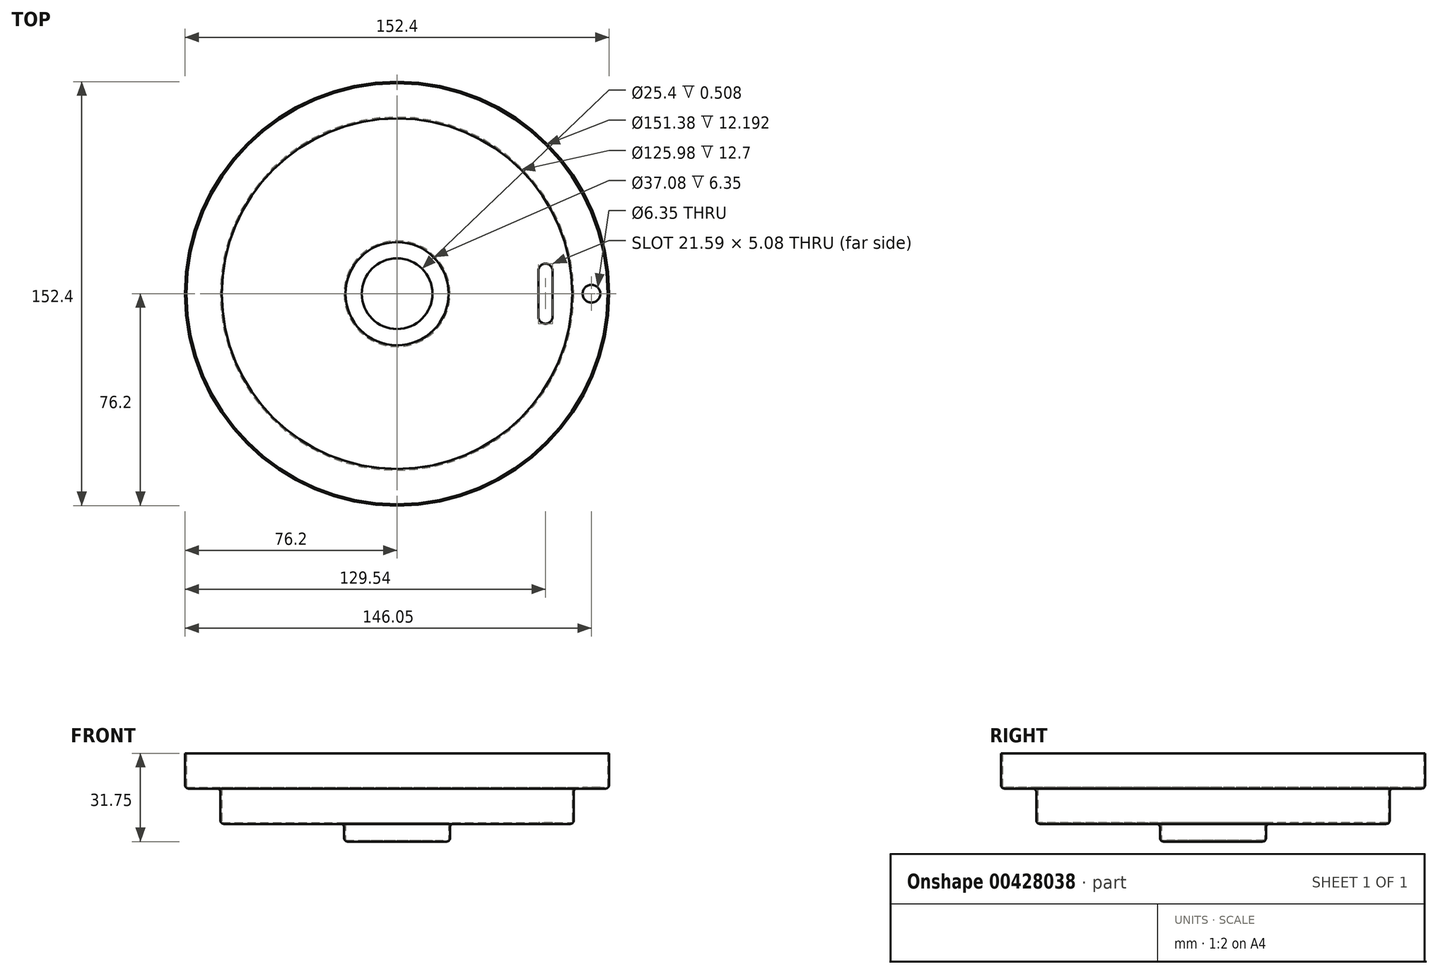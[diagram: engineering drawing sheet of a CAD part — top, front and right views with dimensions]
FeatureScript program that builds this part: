
annotation { "Feature Type Name" : "Feature", "Feature Type Description" : "" }
export const myFeature = defineFeature(function(context is Context, id is Id, definition is map)
    precondition{}
    {
        {
            var Q0;
            Q0=qCreatedBy(makeId("Front.planeOp"),FACE);
            var sketch = newSketch(context, id + "F0", { "sketchPlane" : qUnion([Q0])});
            skLineSegment(sketch, "E0", {"start": v(0, 0) * mm, "end": v(6.35, 0) * mm});
            skLineSegment(sketch, "E1", {"start": v(6.35, 0) * mm, "end": v(6.35, 6.35) * mm});
            skLineSegment(sketch, "E2", {"start": v(6.35, 6.35) * mm, "end": v(50.8, 6.35) * mm});
            skLineSegment(sketch, "E3", {"start": v(50.8, 6.35) * mm, "end": v(50.8, 19.05) * mm});
            skLineSegment(sketch, "E4", {"start": v(50.8, 19.05) * mm, "end": v(63.5, 19.05) * mm});
            skLineSegment(sketch, "E5", {"start": v(63.5, 19.05) * mm, "end": v(63.5, 31.75) * mm});
            skLineSegment(sketch, "E6", {"start": v(63.5, 31.75) * mm, "end": v(63, 31.75) * mm});
            skLineSegment(sketch, "E7", {"start": v(63, 31.75) * mm, "end": v(63, 19.56) * mm});
            skLineSegment(sketch, "E8", {"start": v(63, 19.56) * mm, "end": v(50.3, 19.56) * mm});
            skLineSegment(sketch, "E9", {"start": v(50.3, 19.56) * mm, "end": v(50.3, 6.86) * mm});
            skLineSegment(sketch, "E10", {"start": v(50.3, 6.86) * mm, "end": v(5.84, 6.86) * mm});
            skPoint(sketch, "E11.endSnap0", {"position": v(6.35, 3.18) * mm});
            skLineSegment(sketch, "E12", {"start": v(0, 0.5) * mm, "end": v(0, 0) * mm});
            skLineSegment(sketch, "E13", {"start": v(0, 0.5) * mm, "end": v(5.84, 0.5) * mm});
            skLineSegment(sketch, "E14", {"start": v(5.84, 0.5) * mm, "end": v(5.84, 6.86) * mm});
            skLineSegment(sketch, "E15", {"start": v(0, 0) * mm, "end": v(-12.7, 0) * mm});
            skLineSegment(sketch, "E16", {"start": v(-12.7, 0) * mm, "end": v(-12.7, 12.7) * mm});
            skSolve(sketch);
        }
        {
            var Q0;
            Q0=makeQuery(id+"F0.imprint","IMPRINT",FACE,{"disambiguationData":[TD([[makeQuery(id+"F0.imprint","IMPRINT",EDGE,{"derivedFrom":sQuery(id+"F0.wireOp",EDGE,"E0")}),1.0]])]});
            var Q1;
            Q1=sQuery(id+"F0.wireOp",EDGE,"E16");
            revolve(context, id + "F1", {"entities" : qUnion([Q0]), "axis" : qUnion([Q1]), "revolveType" : RevolveType.FULL});
        }
        {
            var Q0;
            Q0=makeQuery(id+"F1.opRevolve","SWEPT_FACE",FACE,{"disambiguationData":[OSD([sQuery(id+"F0.wireOp",EDGE,"E8")])]});
            var sketch = newSketch(context, id + "F2", { "sketchPlane" : qUnion([Q0])});
            skCircle(sketch, "E17", {"center": v(57.15, 0) * mm, "radius": 3.18 * mm});
            skSolve(sketch);
        }
        {
            var Q0;
            Q0=makeQuery(id+"F2.imprint","IMPRINT",FACE,{"disambiguationData":[TD([[makeQuery(id+"F2.imprint","IMPRINT",EDGE,{"derivedFrom":sQuery(id+"F2.wireOp",EDGE,"E17")}),1.0]])]});
            extrude(context, id + "F3", {"entities" : qUnion([Q0]), "operationType" : NewBodyOperationType.REMOVE, "endBound" : BoundingType.THROUGH_ALL, "oppositeDirection" : true, "depth" : 25.4 * mm});
        }
        {
            var Q0;
            Q0=makeQuery(id+"F1.opRevolve","SWEPT_FACE",FACE,{"disambiguationData":[OSD([sQuery(id+"F0.wireOp",EDGE,"E10")])]});
            var sketch = newSketch(context, id + "F4", { "sketchPlane" : qUnion([Q0])});
            skLineSegment(sketch, "E18", {"start": v(38.1, 0) * mm, "end": v(38.1, 8.26) * mm});
            skLineSegment(sketch, "E19", {"start": v(38.1, 8.26) * mm, "end": v(38.1, -8.26) * mm});
            skLineSegment(sketch, "E20", {"start": v(38.1, -8.26) * mm, "end": v(43.18, -8.26) * mm});
            skLineSegment(sketch, "E21", {"start": v(38.1, 8.26) * mm, "end": v(43.18, 8.26) * mm});
            skLineSegment(sketch, "E22", {"start": v(43.18, 8.26) * mm, "end": v(43.18, -8.26) * mm});
            skArc(sketch, "E23", {"start": v(43.18, 8.26) * mm, "mid": v(40.64, 10.8) * mm, "end": v(38.1, 8.26) * mm});
            skArc(sketch, "E24", {"start": v(38.1, -8.26) * mm, "mid": v(40.64, -10.8) * mm, "end": v(43.18, -8.26) * mm});
            skSolve(sketch);
        }
        {
            var Q0;
            Q0=makeQuery(id+"F4.imprint","IMPRINT",FACE,{"disambiguationData":[TD([[makeQuery(id+"F4.imprint","IMPRINT",EDGE,{"derivedFrom":sQuery(id+"F4.wireOp",EDGE,"E21")}),1.0]])]});
            var Q1;
            {var subQ1=sQuery(id+"F4.wireOp",EDGE,"E20");Q1=makeQuery(id+"F4.imprint","IMPRINT",FACE,{"disambiguationData":[TD([[makeQuery(id+"F4.imprint","IMPRINT",EDGE,{"derivedFrom":subQ1}),1.0]])]});}
            var Q2;
            Q2=makeQuery(id+"F4.imprint","IMPRINT",FACE,{"disambiguationData":[TD([[makeQuery(id+"F4.imprint","IMPRINT",EDGE,{"derivedFrom":sQuery(id+"F4.wireOp",EDGE,"E20")}),-1.0]])]});
            extrude(context, id + "F5", {"entities" : qUnion([Q0, Q1, Q2]), "operationType" : NewBodyOperationType.REMOVE, "endBound" : BoundingType.THROUGH_ALL, "oppositeDirection" : true, "depth" : 25.4 * mm});
        }
        {
            var Q0;
            Q0=makeQuery(id+"F1.opRevolve","SWEPT_EDGE",EDGE,{"disambiguationData":[OSD([sQuery(id+"F0.wireOp",EDGE,"E4"),sQuery(id+"F0.wireOp",EDGE,"E5")])]});
            var Q1;
            Q1=makeQuery(id+"F1.opRevolve","SWEPT_EDGE",EDGE,{"disambiguationData":[OSD([sQuery(id+"F0.wireOp",EDGE,"E3"),sQuery(id+"F0.wireOp",EDGE,"E4")])]});
            var Q2;
            Q2=makeQuery(id+"F1.opRevolve","SWEPT_EDGE",EDGE,{"disambiguationData":[OSD([sQuery(id+"F0.wireOp",EDGE,"E2"),sQuery(id+"F0.wireOp",EDGE,"E3")])]});
            var Q3;
            Q3=makeQuery(id+"F1.opRevolve","SWEPT_EDGE",EDGE,{"disambiguationData":[OSD([sQuery(id+"F0.wireOp",EDGE,"E1"),sQuery(id+"F0.wireOp",EDGE,"E2")])]});
            var Q4;
            Q4=makeQuery(id+"F1.opRevolve","SWEPT_EDGE",EDGE,{"disambiguationData":[OSD([sQuery(id+"F0.wireOp",EDGE,"E0"),sQuery(id+"F0.wireOp",EDGE,"E1")])]});
            fillet(context, id + "F6", {"entities" : qUnion([Q0, Q1, Q2, Q3, Q4]), "radius" : 1.27 * mm, "tangentPropagation" : true, "allowEdgeOverflow" : false});
        }
    });
